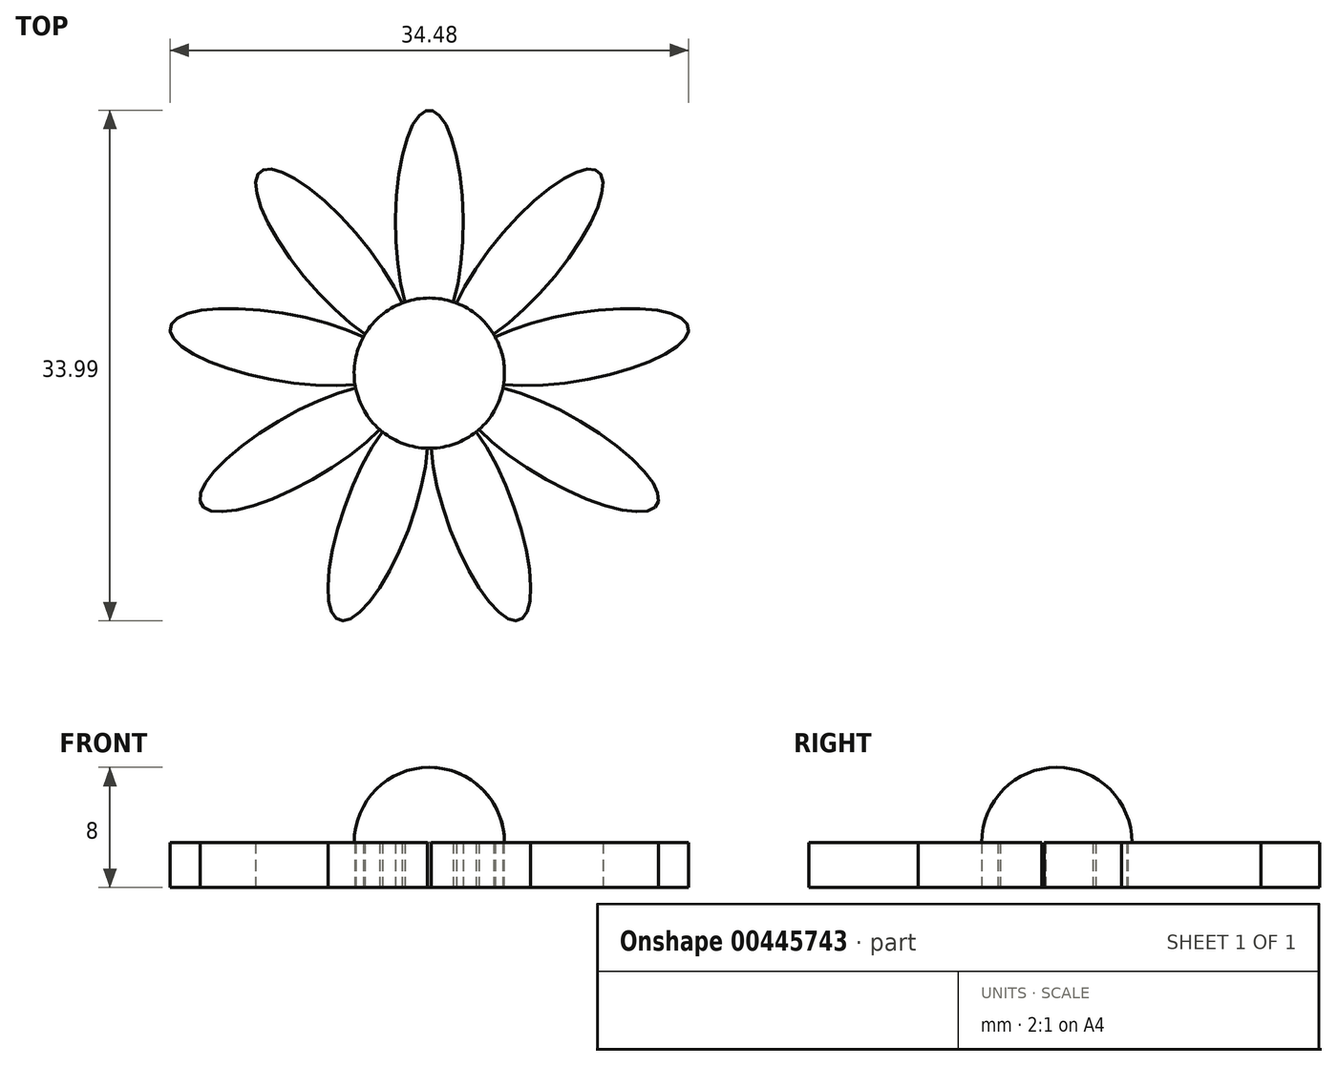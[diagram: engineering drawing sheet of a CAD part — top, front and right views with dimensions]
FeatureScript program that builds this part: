
annotation { "Feature Type Name" : "Feature", "Feature Type Description" : "" }
export const myFeature = defineFeature(function(context is Context, id is Id, definition is map)
    precondition{}
    {
        {
            var Q0;
            Q0=qCreatedBy(makeId("Top.planeOp"),FACE);
            var sketch = newSketch(context, id + "F0", { "sketchPlane" : qUnion([Q0])});
            skCircle(sketch, "E0", {"center": v(0, 0) * mm, "radius": 5 * mm});
            skLineSegment(sketch, "E1", {"start": v(0, 0) * mm, "end": v(0, 10) * mm, "construction": true});
            skEllipse(sketch, "E2", {"center": v(0, 10) * mm, "majorRadius": 7.5 * mm, "minorRadius": 2.25 * mm, "majorAxis": v(0, -1)});
            skEllipse(sketch, "E3.1.0", {"center": v(-6.43, 7.66) * mm, "majorRadius": 7.5 * mm, "minorRadius": 2.25 * mm, "majorAxis": v(0.64, -0.77)});
            skEllipse(sketch, "E3.2.0", {"center": v(-9.85, 1.74) * mm, "majorRadius": 7.5 * mm, "minorRadius": 2.25 * mm, "majorAxis": v(0.98, -0.17)});
            skEllipse(sketch, "E3.3.0", {"center": v(-8.66, -5) * mm, "majorRadius": 7.5 * mm, "minorRadius": 2.25 * mm, "majorAxis": v(0.87, 0.5)});
            skEllipse(sketch, "E3.4.0", {"center": v(-3.42, -9.4) * mm, "majorRadius": 7.5 * mm, "minorRadius": 2.25 * mm, "majorAxis": v(0.34, 0.94)});
            skEllipse(sketch, "E3.5.0", {"center": v(3.42, -9.4) * mm, "majorRadius": 7.5 * mm, "minorRadius": 2.25 * mm, "majorAxis": v(-0.34, 0.94)});
            skEllipse(sketch, "E3.6.0", {"center": v(8.66, -5) * mm, "majorRadius": 7.5 * mm, "minorRadius": 2.25 * mm, "majorAxis": v(-0.87, 0.5)});
            skEllipse(sketch, "E3.7.0", {"center": v(9.85, 1.74) * mm, "majorRadius": 7.5 * mm, "minorRadius": 2.25 * mm, "majorAxis": v(-0.98, -0.17)});
            skEllipse(sketch, "E3.8.0", {"center": v(6.43, 7.66) * mm, "majorRadius": 7.5 * mm, "minorRadius": 2.25 * mm, "majorAxis": v(-0.64, -0.77)});
            skSolve(sketch);
        }
        {
            var Q0;
            Q0 = qSketchRegion(id + "F0", true);
            extrude(context, id + "F1", {"entities" : qUnion([Q0]), "depth" : 3 * mm});
        }
        {
            var Q0;
            Q0=makeQuery(id+"F1.opExtrude","CAP_FACE",FACE,{"disambiguationData":[OSD([sQuery(id+"F0.wireOp",EDGE,"E0"),sQuery(id+"F0.wireOp",EDGE,"E2"),sQuery(id+"F0.wireOp",EDGE,"E3.1.0"),sQuery(id+"F0.wireOp",EDGE,"E3.2.0"),sQuery(id+"F0.wireOp",EDGE,"E3.3.0"),sQuery(id+"F0.wireOp",EDGE,"E3.4.0"),sQuery(id+"F0.wireOp",EDGE,"E3.5.0"),sQuery(id+"F0.wireOp",EDGE,"E3.6.0"),sQuery(id+"F0.wireOp",EDGE,"E3.7.0"),sQuery(id+"F0.wireOp",EDGE,"E3.8.0")])],"isStart":false});
            var sketch = newSketch(context, id + "F2", { "sketchPlane" : qUnion([Q0])});
            skCircle(sketch, "E4", {"center": v(0, 0) * mm, "radius": 5 * mm});
            skSolve(sketch);
        }
        {
            var Q0;
            {var subQ0=sQuery(id+"F2.wireOp",EDGE,"E4");var subQ12=makeQuery(id+"F1.opExtrude","CAP_EDGE",EDGE,{"disambiguationData":[OSD([sQuery(id+"F0.wireOp",EDGE,"E3.8.0")])],"isStart":false});var subQ13=makeQuery(id+"F2.imprint","INTERSECT",VERTEX,{"disambiguationData":[OD(0.0)],"derivedFrom":[subQ12,subQ0]});Q0=makeQuery(id+"F2.imprint","IMPRINT",FACE,{"disambiguationData":[TD([[makeQuery(id+"F2.imprint","IMPRINT",EDGE,{"disambiguationData":[TD([[subQ13,1.0]])],"derivedFrom":subQ0}),1.0]])]});}
            extrude(context, id + "F3", {"entities" : qUnion([Q0]), "operationType" : NewBodyOperationType.ADD, "depth" : 5 * mm});
        }
        {
            var Q0;
            Q0=makeQuery(id+"F3.opExtrude","CAP_EDGE",EDGE,{"disambiguationData":[OSD([sQuery(id+"F2.wireOp",EDGE,"E4")])],"isStart":false});
            fillet(context, id + "F4", {"entities" : qUnion([Q0]), "radius" : 5 * mm, "tangentPropagation" : true, "allowEdgeOverflow" : false});
        }
    });
